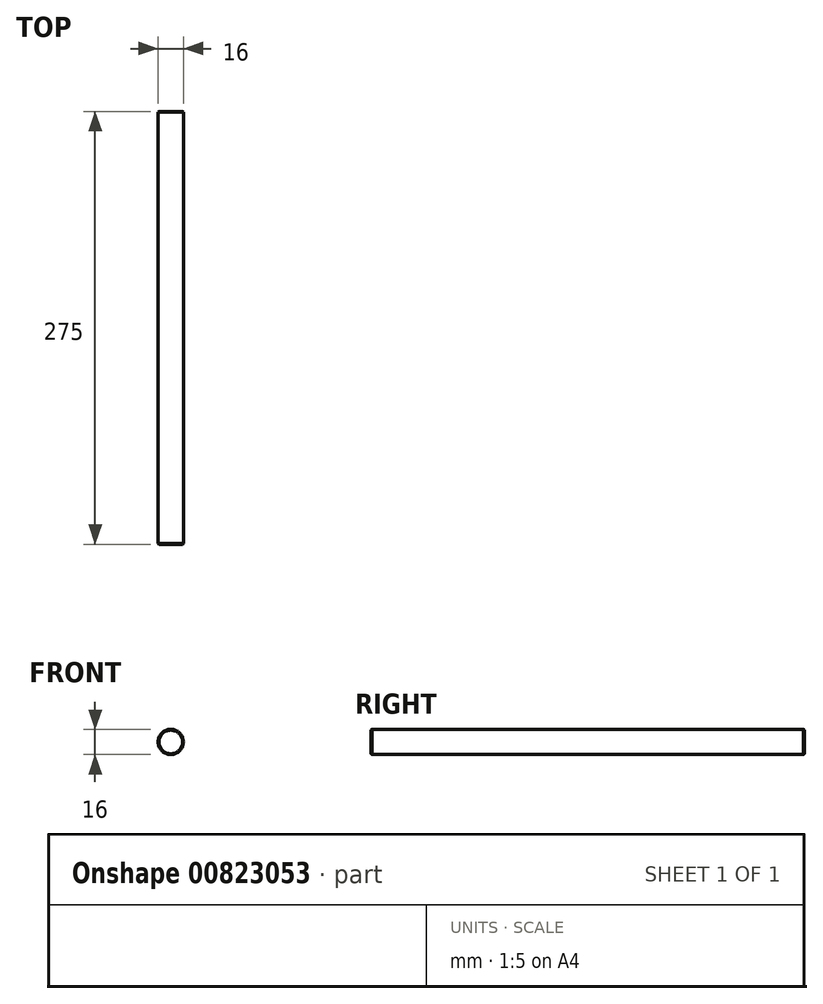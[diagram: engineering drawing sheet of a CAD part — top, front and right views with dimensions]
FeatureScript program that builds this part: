
annotation { "Feature Type Name" : "Feature", "Feature Type Description" : "" }
export const myFeature = defineFeature(function(context is Context, id is Id, definition is map)
    precondition{}
    {
        {
            var Q0;
            Q0=qCreatedBy(makeId("Front.planeOp"),FACE);
            var sketch = newSketch(context, id + "F0", { "sketchPlane" : qUnion([Q0])});
            skCircle(sketch, "E0", {"center": v(0, 0) * mm, "radius": 8 * mm});
            skSolve(sketch);
        }
        {
            var Q0;
            Q0=qSketchRegion(id+"F0",true);
            extrude(context, id + "F1", {"entities" : qUnion([Q0]), "endBound" : BoundingType.SYMMETRIC, "depth" : 275 * mm, "offsetDistance" : 25 * mm});
        }
        {
            var Q0;
            Q0=makeQuery(id+"F1.opExtrude","SWEPT_FACE",FACE,{"disambiguationData":[OSD([sQuery(id+"F0.wireOp",EDGE,"E0")])]});
            chamfer(context, id + "F2", {"entities" : qUnion([Q0]), "width" : 0.5 * mm, "tangentPropagation" : true});
        }
    });
